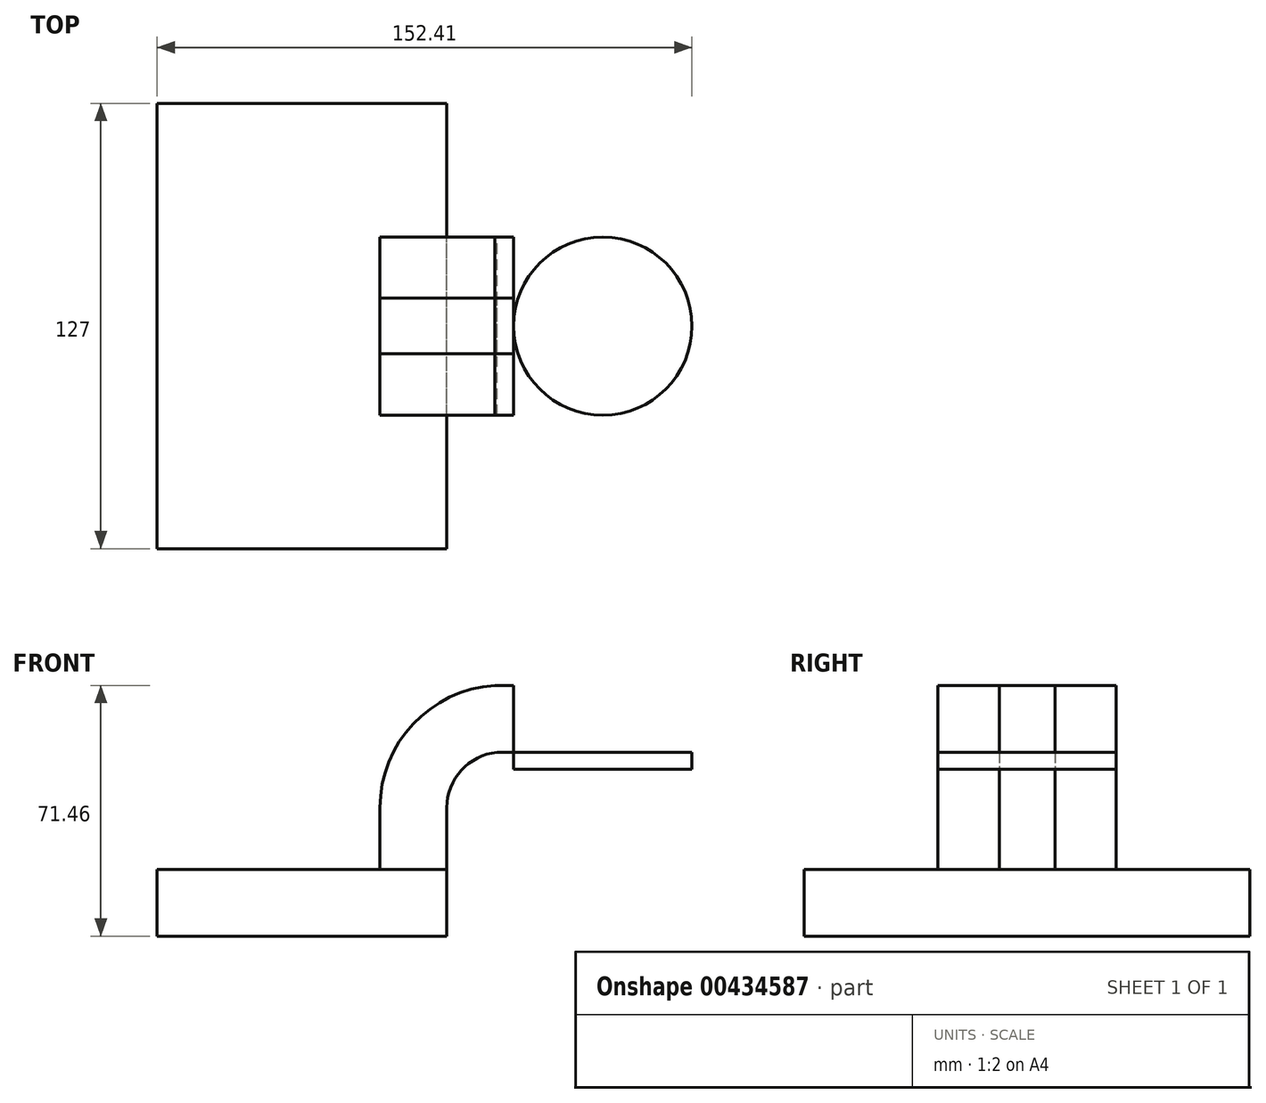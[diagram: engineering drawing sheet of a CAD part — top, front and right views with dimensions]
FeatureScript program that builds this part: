
annotation { "Feature Type Name" : "Feature", "Feature Type Description" : "" }
export const myFeature = defineFeature(function(context is Context, id is Id, definition is map)
    precondition{}
    {
        {
            var Q0;
            Q0=qCreatedBy(makeId("Front.planeOp"),FACE);
            var sketch = newSketch(context, id + "F0", { "sketchPlane" : qUnion([Q0])});
            skLineSegment(sketch, "E0.bottom", {"start": v(41.28, -9.52) * mm, "end": v(-41.28, -9.53) * mm});
            skLineSegment(sketch, "E0.top", {"start": v(41.28, 9.53) * mm, "end": v(-41.28, 9.53) * mm});
            skLineSegment(sketch, "E0.left", {"start": v(41.28, -9.52) * mm, "end": v(41.28, 9.53) * mm});
            skLineSegment(sketch, "E0.right", {"start": v(-41.28, -9.52) * mm, "end": v(-41.28, 9.53) * mm});
            skPoint(sketch, "E0.middle", {"position": v(0, 0) * mm});
            skLineSegment(sketch, "E1.bottom", {"start": v(111.12, 38.1) * mm, "end": v(60.32, 38.1) * mm});
            skLineSegment(sketch, "E1.top", {"start": v(111.12, 66.68) * mm, "end": v(60.32, 66.68) * mm});
            skLineSegment(sketch, "E1.left", {"start": v(111.12, 38.1) * mm, "end": v(111.12, 66.68) * mm});
            skLineSegment(sketch, "E1.right", {"start": v(60.32, 38.1) * mm, "end": v(60.32, 66.68) * mm});
            skPoint(sketch, "E1.middle", {"position": v(85.72, 52.39) * mm});
            skLineSegment(sketch, "E2", {"start": v(41.28, 9.53) * mm, "end": v(41.28, 27.07) * mm});
            skArc(sketch, "E3", {"start": v(41.27, 27.07) * mm, "mid": v(45.4, 37.75) * mm, "end": v(55.64, 42.88) * mm});
            skLineSegment(sketch, "E4", {"start": v(55.64, 42.88) * mm, "end": v(85.72, 42.88) * mm});
            skLineSegment(sketch, "E5.0", {"start": v(54.9, 61.93) * mm, "end": v(85.72, 61.93) * mm});
            skArc(sketch, "E5.1", {"start": v(22.22, 27.07) * mm, "mid": v(31.67, 50.96) * mm, "end": v(54.9, 61.93) * mm});
            skLineSegment(sketch, "E5.2", {"start": v(22.22, 9.53) * mm, "end": v(22.22, 27.07) * mm});
            skFitSpline(sketch, "E6", {"points": [v(-41.28, 9.52) * mm, v(54.9, 61.93) * mm], "startDerivative": vector(90.9, 142.38) * mm, "endDerivative": vector(87.69, -2.24) * mm});
            skLineSegment(sketch, "E7", {"start": v(85.72, 61.93) * mm, "end": v(85.72, 42.88) * mm});
            skLineSegment(sketch, "E8", {"start": v(85.72, 66.68) * mm, "end": v(85.72, 52.39) * mm});
            skLineSegment(sketch, "E9", {"start": v(85.72, 38.1) * mm, "end": v(85.72, 52.39) * mm});
            skSolve(sketch);
        }
        {
            var Q0;
            Q0=makeQuery(id+"F0.imprint","IMPRINT",FACE,{"disambiguationData":[TD([[makeQuery(id+"F0.imprint","IMPRINT",EDGE,{"derivedFrom":sQuery(id+"F0.wireOp",EDGE,"E0.bottom")}),-1.0]])]});
            extrude(context, id + "F1", {"entities" : qUnion([Q0]), "endBound" : BoundingType.SYMMETRIC, "depth" : 127 * mm});
        }
        {
            var Q0;
            {var subQ1=sQuery(id+"F0.wireOp",EDGE,"E2");Q0=makeQuery(id+"F0.imprint","IMPRINT",FACE,{"disambiguationData":[TD([[makeQuery(id+"F0.imprint","IMPRINT",EDGE,{"derivedFrom":subQ1}),1.0]])]});}
            extrude(context, id + "F2", {"entities" : qUnion([Q0]), "endBound" : BoundingType.SYMMETRIC, "depth" : 50.8 * mm});
        }
        {
            var Q0;
            Q0=makeQuery(id+"F0.imprint","IMPRINT",FACE,{"disambiguationData":[TD([[makeQuery(id+"F0.imprint","IMPRINT",EDGE,{"derivedFrom":sQuery(id+"F0.wireOp",EDGE,"E5.1")}),1.0]])]});
            extrude(context, id + "F3", {"entities" : qUnion([Q0]), "endBound" : BoundingType.SYMMETRIC, "depth" : 15.88 * mm});
        }
        {
            var Q0;
            {var subQ1=sQuery(id+"F0.wireOp",EDGE,"E1.bottom");Q0=makeQuery(id+"F0.imprint","IMPRINT",FACE,{"disambiguationData":[TD([[makeQuery(id+"F0.imprint","IMPRINT",EDGE,{"derivedFrom":subQ1}),-1.0]])]});}
            var Q1;
            Q1=sQuery(id+"F0.wireOp",EDGE,"E7");
            revolve(context, id + "F4", {"entities" : qUnion([Q0]), "axis" : qUnion([Q1]), "revolveType" : RevolveType.FULL});
        }
    });
